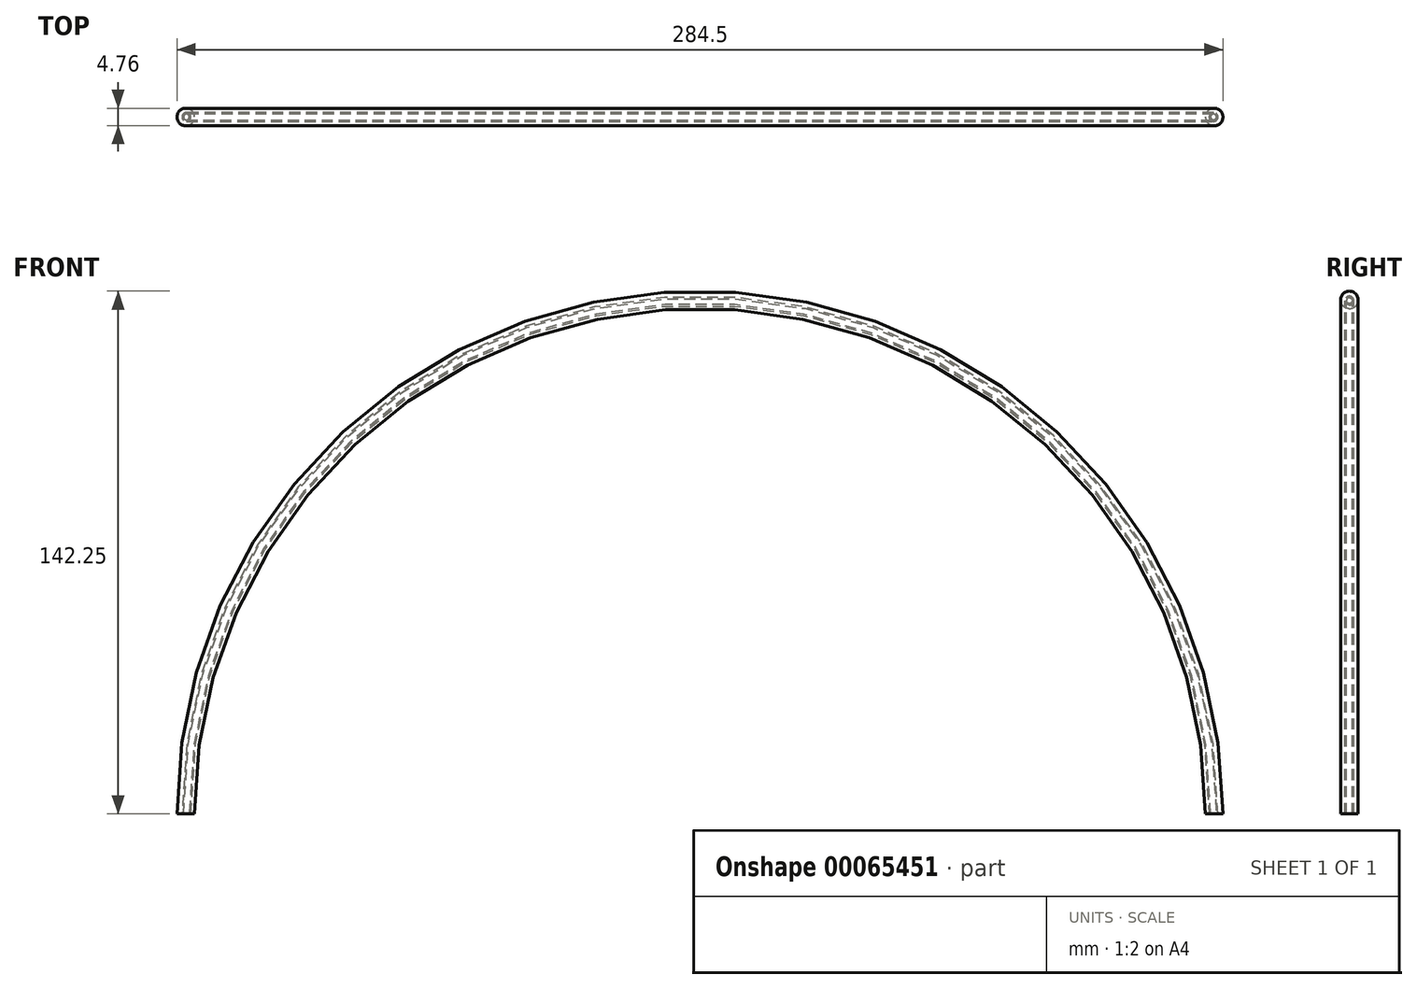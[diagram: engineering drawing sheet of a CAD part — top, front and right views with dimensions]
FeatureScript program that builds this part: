
annotation { "Feature Type Name" : "Feature", "Feature Type Description" : "" }
export const myFeature = defineFeature(function(context is Context, id is Id, definition is map)
    precondition{}
    {
        {
            var Q0;
            Q0=qCreatedBy(makeId("Front.planeOp"),FACE);
            var sketch = newSketch(context, id + "F0", { "sketchPlane" : qUnion([Q0])});
            skArc(sketch, "E0", {"start": v(-139.7, 0) * mm, "mid": v(0, 139.7) * mm, "end": v(139.7, 0) * mm});
            skSolve(sketch);
        }
        {
            var Q0;
            Q0=qCreatedBy(makeId("Top.planeOp"),FACE);
            var sketch = newSketch(context, id + "F1", { "sketchPlane" : qUnion([Q0])});
            skCircle(sketch, "E1", {"center": v(-139.87, 0) * mm, "radius": 2.38 * mm});
            skSolve(sketch);
        }
        {
            var Q0;
            Q0=makeQuery(id+"F1.imprint","IMPRINT",FACE,{"disambiguationData":[TD([[makeQuery(id+"F1.imprint","IMPRINT",EDGE,{"derivedFrom":sQuery(id+"F1.wireOp",EDGE,"E1")}),1.0]])]});
            var Q1;
            Q1=sQuery(id+"F0.wireOp",EDGE,"E0");
            sweep(context, id + "F2", {"profiles" : qUnion([Q0]), "path" : qUnion([Q1])});
        }
        {
            var Q0;
            Q0=qCreatedBy(makeId("Top.planeOp"),FACE);
            var sketch = newSketch(context, id + "F3", { "sketchPlane" : qUnion([Q0])});
            skCircle(sketch, "E2", {"center": v(-139.68, 0) * mm, "radius": 1.2 * mm});
            skSolve(sketch);
        }
        {
            var Q0;
            Q0=makeQuery(id+"F3.imprint","IMPRINT",FACE,{"disambiguationData":[TD([[makeQuery(id+"F3.imprint","IMPRINT",EDGE,{"derivedFrom":sQuery(id+"F3.wireOp",EDGE,"E2")}),1.0]])]});
            var Q1;
            Q1=sQuery(id+"F0.wireOp",EDGE,"E0");
            sweep(context, id + "F4", {"operationType" : NewBodyOperationType.REMOVE, "profiles" : qUnion([Q0]), "path" : qUnion([Q1])});
        }
        {
            var Q0;
            Q0=makeQuery(id+"F2.opSweep","CAP_FACE",FACE,{"disambiguationData":[OSD([sQuery(id+"F0.wireOp",VERTEX,"E0.start"),sQuery(id+"F1.wireOp",EDGE,"E1")])],"isStart":true});
            var sketch = newSketch(context, id + "F5", { "sketchPlane" : qUnion([Q0])});
            skCircle(sketch, "E3", {"center": v(-139.68, 0) * mm, "radius": 0.8 * mm});
            skSolve(sketch);
        }
        {
            var Q0;
            Q0=makeQuery(id+"F5.imprint","IMPRINT",FACE,{"disambiguationData":[TD([[makeQuery(id+"F5.imprint","IMPRINT",EDGE,{"derivedFrom":sQuery(id+"F5.wireOp",EDGE,"E3")}),1.0]])]});
            var Q1;
            Q1=sQuery(id+"F0.wireOp",EDGE,"E0");
            sweep(context, id + "F6", {"profiles" : qUnion([Q0]), "path" : qUnion([Q1])});
        }
    });
